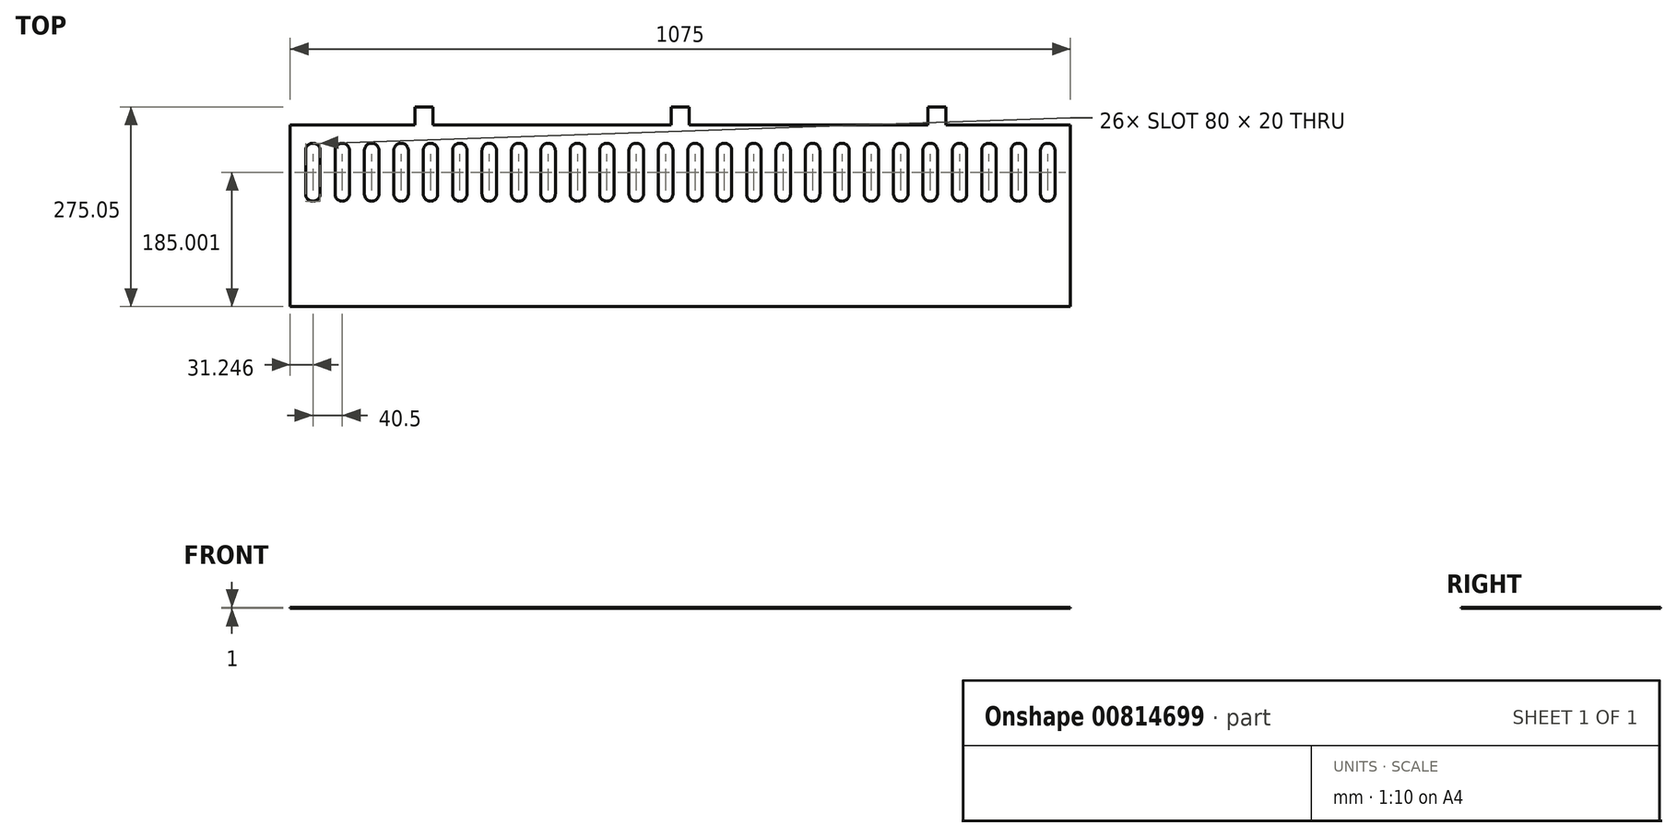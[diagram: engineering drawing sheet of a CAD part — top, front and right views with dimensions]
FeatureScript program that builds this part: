
annotation { "Feature Type Name" : "Feature", "Feature Type Description" : "" }
export const myFeature = defineFeature(function(context is Context, id is Id, definition is map)
    precondition{}
    {
        {
            var Q0;
            Q0=qCreatedBy(makeId("Top.planeOp"),FACE);
            var sketch = newSketch(context, id + "F0", { "sketchPlane" : qUnion([Q0])});
            skLineSegment(sketch, "E0.bottom", {"start": v(-117.32, -164.64) * mm, "end": v(957.68, -164.64) * mm});
            skLineSegment(sketch, "E0.top", {"start": v(-117.32, -414.64) * mm, "end": v(957.68, -414.64) * mm});
            skLineSegment(sketch, "E0.left", {"start": v(-117.32, -164.64) * mm, "end": v(-117.32, -414.64) * mm});
            skLineSegment(sketch, "E0.right", {"start": v(957.68, -164.64) * mm, "end": v(957.68, -414.64) * mm});
            skArc(sketch, "E1", {"start": v(-76.07, -199.64) * mm, "mid": v(-86.07, -189.64) * mm, "end": v(-96.07, -199.64) * mm});
            skArc(sketch, "E2", {"start": v(-96.07, -259.64) * mm, "mid": v(-86.07, -269.64) * mm, "end": v(-76.07, -259.64) * mm});
            skLineSegment(sketch, "E3", {"start": v(-96.07, -199.64) * mm, "end": v(-96.07, -259.64) * mm});
            skLineSegment(sketch, "E4", {"start": v(-76.07, -199.64) * mm, "end": v(-76.07, -259.64) * mm});
            skArc(sketch, "E5", {"start": v(-35.57, -199.64) * mm, "mid": v(-45.57, -189.64) * mm, "end": v(-55.57, -199.64) * mm});
            skArc(sketch, "E6", {"start": v(-55.57, -259.64) * mm, "mid": v(-45.57, -269.64) * mm, "end": v(-35.57, -259.64) * mm});
            skLineSegment(sketch, "E7", {"start": v(-55.57, -199.64) * mm, "end": v(-55.57, -259.64) * mm});
            skLineSegment(sketch, "E8", {"start": v(-35.57, -199.64) * mm, "end": v(-35.57, -259.64) * mm});
            skArc(sketch, "E9", {"start": v(4.93, -199.64) * mm, "mid": v(-5.07, -189.64) * mm, "end": v(-15.07, -199.64) * mm});
            skArc(sketch, "E10", {"start": v(-15.07, -259.64) * mm, "mid": v(-5.07, -269.64) * mm, "end": v(4.93, -259.64) * mm});
            skLineSegment(sketch, "E11", {"start": v(-15.07, -199.64) * mm, "end": v(-15.07, -259.64) * mm});
            skLineSegment(sketch, "E12", {"start": v(4.93, -199.64) * mm, "end": v(4.93, -259.64) * mm});
            skArc(sketch, "E13", {"start": v(45.43, -199.64) * mm, "mid": v(35.43, -189.64) * mm, "end": v(25.43, -199.64) * mm});
            skArc(sketch, "E14", {"start": v(25.43, -259.64) * mm, "mid": v(35.43, -269.64) * mm, "end": v(45.43, -259.64) * mm});
            skLineSegment(sketch, "E15", {"start": v(25.43, -199.64) * mm, "end": v(25.43, -259.64) * mm});
            skLineSegment(sketch, "E16", {"start": v(45.43, -199.64) * mm, "end": v(45.43, -259.64) * mm});
            skArc(sketch, "E17", {"start": v(85.93, -199.64) * mm, "mid": v(75.93, -189.64) * mm, "end": v(65.93, -199.64) * mm});
            skArc(sketch, "E18", {"start": v(65.93, -259.64) * mm, "mid": v(75.93, -269.64) * mm, "end": v(85.93, -259.64) * mm});
            skLineSegment(sketch, "E19", {"start": v(65.93, -199.64) * mm, "end": v(65.93, -259.64) * mm});
            skLineSegment(sketch, "E20", {"start": v(85.93, -199.64) * mm, "end": v(85.93, -259.64) * mm});
            skArc(sketch, "E21", {"start": v(126.43, -199.64) * mm, "mid": v(116.43, -189.64) * mm, "end": v(106.43, -199.64) * mm});
            skArc(sketch, "E22", {"start": v(106.43, -259.64) * mm, "mid": v(116.43, -269.64) * mm, "end": v(126.43, -259.64) * mm});
            skLineSegment(sketch, "E23", {"start": v(106.43, -199.64) * mm, "end": v(106.43, -259.64) * mm});
            skLineSegment(sketch, "E24", {"start": v(126.43, -199.64) * mm, "end": v(126.43, -259.64) * mm});
            skArc(sketch, "E25", {"start": v(207.43, -199.64) * mm, "mid": v(197.43, -189.64) * mm, "end": v(187.43, -199.64) * mm});
            skArc(sketch, "E26", {"start": v(187.43, -259.64) * mm, "mid": v(197.43, -269.64) * mm, "end": v(207.43, -259.64) * mm});
            skLineSegment(sketch, "E27", {"start": v(187.43, -199.64) * mm, "end": v(187.43, -259.64) * mm});
            skLineSegment(sketch, "E28", {"start": v(207.43, -199.64) * mm, "end": v(207.43, -259.64) * mm});
            skArc(sketch, "E29", {"start": v(247.93, -199.64) * mm, "mid": v(237.93, -189.64) * mm, "end": v(227.93, -199.64) * mm});
            skArc(sketch, "E30", {"start": v(227.93, -259.64) * mm, "mid": v(237.93, -269.64) * mm, "end": v(247.93, -259.64) * mm});
            skLineSegment(sketch, "E31", {"start": v(227.93, -199.64) * mm, "end": v(227.93, -259.64) * mm});
            skLineSegment(sketch, "E32", {"start": v(247.93, -199.64) * mm, "end": v(247.93, -259.64) * mm});
            skArc(sketch, "E33", {"start": v(288.43, -199.64) * mm, "mid": v(278.43, -189.64) * mm, "end": v(268.43, -199.64) * mm});
            skArc(sketch, "E34", {"start": v(268.43, -259.64) * mm, "mid": v(278.43, -269.64) * mm, "end": v(288.43, -259.64) * mm});
            skLineSegment(sketch, "E35", {"start": v(268.43, -199.64) * mm, "end": v(268.43, -259.64) * mm});
            skLineSegment(sketch, "E36", {"start": v(288.43, -199.64) * mm, "end": v(288.43, -259.64) * mm});
            skArc(sketch, "E37", {"start": v(328.93, -199.64) * mm, "mid": v(318.93, -189.64) * mm, "end": v(308.93, -199.64) * mm});
            skArc(sketch, "E38", {"start": v(308.93, -259.64) * mm, "mid": v(318.93, -269.64) * mm, "end": v(328.93, -259.64) * mm});
            skLineSegment(sketch, "E39", {"start": v(308.93, -199.64) * mm, "end": v(308.93, -259.64) * mm});
            skLineSegment(sketch, "E40", {"start": v(328.93, -199.64) * mm, "end": v(328.93, -259.64) * mm});
            skArc(sketch, "E41", {"start": v(369.43, -199.64) * mm, "mid": v(359.43, -189.64) * mm, "end": v(349.43, -199.64) * mm});
            skArc(sketch, "E42", {"start": v(349.43, -259.64) * mm, "mid": v(359.43, -269.64) * mm, "end": v(369.43, -259.64) * mm});
            skLineSegment(sketch, "E43", {"start": v(349.43, -199.64) * mm, "end": v(349.43, -259.64) * mm});
            skLineSegment(sketch, "E44", {"start": v(369.43, -199.64) * mm, "end": v(369.43, -259.64) * mm});
            skArc(sketch, "E45", {"start": v(409.93, -199.64) * mm, "mid": v(399.93, -189.64) * mm, "end": v(389.93, -199.64) * mm});
            skArc(sketch, "E46", {"start": v(389.93, -259.64) * mm, "mid": v(399.93, -269.64) * mm, "end": v(409.93, -259.64) * mm});
            skLineSegment(sketch, "E47", {"start": v(389.93, -199.64) * mm, "end": v(389.93, -259.64) * mm});
            skLineSegment(sketch, "E48", {"start": v(409.93, -199.64) * mm, "end": v(409.93, -259.64) * mm});
            skArc(sketch, "E49", {"start": v(450.43, -199.64) * mm, "mid": v(440.43, -189.64) * mm, "end": v(430.43, -199.64) * mm});
            skArc(sketch, "E50", {"start": v(430.43, -259.64) * mm, "mid": v(440.43, -269.64) * mm, "end": v(450.43, -259.64) * mm});
            skLineSegment(sketch, "E51", {"start": v(430.43, -199.64) * mm, "end": v(430.43, -259.64) * mm});
            skLineSegment(sketch, "E52", {"start": v(450.43, -199.64) * mm, "end": v(450.43, -259.64) * mm});
            skArc(sketch, "E53", {"start": v(490.93, -199.64) * mm, "mid": v(480.93, -189.64) * mm, "end": v(470.93, -199.64) * mm});
            skArc(sketch, "E54", {"start": v(470.93, -259.64) * mm, "mid": v(480.93, -269.64) * mm, "end": v(490.93, -259.64) * mm});
            skLineSegment(sketch, "E55", {"start": v(470.93, -199.64) * mm, "end": v(470.93, -259.64) * mm});
            skLineSegment(sketch, "E56", {"start": v(490.93, -199.64) * mm, "end": v(490.93, -259.64) * mm});
            skArc(sketch, "E57", {"start": v(531.43, -199.64) * mm, "mid": v(521.43, -189.64) * mm, "end": v(511.43, -199.64) * mm});
            skArc(sketch, "E58", {"start": v(511.43, -259.64) * mm, "mid": v(521.43, -269.64) * mm, "end": v(531.43, -259.64) * mm});
            skLineSegment(sketch, "E59", {"start": v(511.43, -199.64) * mm, "end": v(511.43, -259.64) * mm});
            skLineSegment(sketch, "E60", {"start": v(531.43, -199.64) * mm, "end": v(531.43, -259.64) * mm});
            skArc(sketch, "E61", {"start": v(166.93, -199.64) * mm, "mid": v(156.93, -189.64) * mm, "end": v(146.93, -199.64) * mm});
            skArc(sketch, "E62", {"start": v(146.93, -259.64) * mm, "mid": v(156.93, -269.64) * mm, "end": v(166.93, -259.64) * mm});
            skLineSegment(sketch, "E63", {"start": v(146.93, -199.64) * mm, "end": v(146.93, -259.64) * mm});
            skLineSegment(sketch, "E64", {"start": v(166.93, -199.64) * mm, "end": v(166.93, -259.64) * mm});
            skArc(sketch, "E65", {"start": v(612.43, -199.64) * mm, "mid": v(602.43, -189.64) * mm, "end": v(592.43, -199.64) * mm});
            skArc(sketch, "E66", {"start": v(592.43, -259.64) * mm, "mid": v(602.43, -269.64) * mm, "end": v(612.43, -259.64) * mm});
            skLineSegment(sketch, "E67", {"start": v(592.43, -199.64) * mm, "end": v(592.43, -259.64) * mm});
            skLineSegment(sketch, "E68", {"start": v(612.43, -199.64) * mm, "end": v(612.43, -259.64) * mm});
            skArc(sketch, "E69", {"start": v(652.93, -199.64) * mm, "mid": v(642.93, -189.64) * mm, "end": v(632.93, -199.64) * mm});
            skArc(sketch, "E70", {"start": v(632.93, -259.64) * mm, "mid": v(642.93, -269.64) * mm, "end": v(652.93, -259.64) * mm});
            skLineSegment(sketch, "E71", {"start": v(632.93, -199.64) * mm, "end": v(632.93, -259.64) * mm});
            skLineSegment(sketch, "E72", {"start": v(652.93, -199.64) * mm, "end": v(652.93, -259.64) * mm});
            skArc(sketch, "E73", {"start": v(693.43, -199.64) * mm, "mid": v(683.43, -189.64) * mm, "end": v(673.43, -199.64) * mm});
            skArc(sketch, "E74", {"start": v(673.43, -259.64) * mm, "mid": v(683.43, -269.64) * mm, "end": v(693.43, -259.64) * mm});
            skLineSegment(sketch, "E75", {"start": v(673.43, -199.64) * mm, "end": v(673.43, -259.64) * mm});
            skLineSegment(sketch, "E76", {"start": v(693.43, -199.64) * mm, "end": v(693.43, -259.64) * mm});
            skArc(sketch, "E77", {"start": v(733.93, -199.64) * mm, "mid": v(723.93, -189.64) * mm, "end": v(713.93, -199.64) * mm});
            skArc(sketch, "E78", {"start": v(713.93, -259.64) * mm, "mid": v(723.93, -269.64) * mm, "end": v(733.93, -259.64) * mm});
            skLineSegment(sketch, "E79", {"start": v(713.93, -199.64) * mm, "end": v(713.93, -259.64) * mm});
            skArc(sketch, "E80", {"start": v(774.43, -199.64) * mm, "mid": v(764.43, -189.64) * mm, "end": v(754.43, -199.64) * mm});
            skArc(sketch, "E81", {"start": v(754.43, -259.64) * mm, "mid": v(764.43, -269.64) * mm, "end": v(774.43, -259.64) * mm});
            skLineSegment(sketch, "E82", {"start": v(754.43, -199.64) * mm, "end": v(754.43, -259.64) * mm});
            skLineSegment(sketch, "E83", {"start": v(774.43, -199.64) * mm, "end": v(774.43, -259.64) * mm});
            skArc(sketch, "E84", {"start": v(814.93, -199.64) * mm, "mid": v(804.93, -189.64) * mm, "end": v(794.93, -199.64) * mm});
            skArc(sketch, "E85", {"start": v(794.93, -259.64) * mm, "mid": v(804.93, -269.64) * mm, "end": v(814.93, -259.64) * mm});
            skLineSegment(sketch, "E86", {"start": v(794.93, -199.64) * mm, "end": v(794.93, -259.64) * mm});
            skLineSegment(sketch, "E87", {"start": v(814.93, -199.64) * mm, "end": v(814.93, -259.64) * mm});
            skArc(sketch, "E88", {"start": v(855.43, -199.64) * mm, "mid": v(845.43, -189.64) * mm, "end": v(835.43, -199.64) * mm});
            skArc(sketch, "E89", {"start": v(835.43, -259.64) * mm, "mid": v(845.43, -269.64) * mm, "end": v(855.43, -259.64) * mm});
            skLineSegment(sketch, "E90", {"start": v(835.43, -199.64) * mm, "end": v(835.43, -259.64) * mm});
            skLineSegment(sketch, "E91", {"start": v(855.43, -199.64) * mm, "end": v(855.43, -259.64) * mm});
            skArc(sketch, "E92", {"start": v(895.93, -199.64) * mm, "mid": v(885.93, -189.64) * mm, "end": v(875.93, -199.64) * mm});
            skArc(sketch, "E93", {"start": v(875.93, -259.64) * mm, "mid": v(885.93, -269.64) * mm, "end": v(895.93, -259.64) * mm});
            skLineSegment(sketch, "E94", {"start": v(875.93, -199.64) * mm, "end": v(875.93, -259.64) * mm});
            skLineSegment(sketch, "E95", {"start": v(895.93, -199.64) * mm, "end": v(895.93, -259.64) * mm});
            skArc(sketch, "E96", {"start": v(936.43, -199.64) * mm, "mid": v(926.43, -189.64) * mm, "end": v(916.43, -199.64) * mm});
            skArc(sketch, "E97", {"start": v(916.43, -259.64) * mm, "mid": v(926.43, -269.64) * mm, "end": v(936.43, -259.64) * mm});
            skLineSegment(sketch, "E98", {"start": v(916.43, -199.64) * mm, "end": v(916.43, -259.64) * mm});
            skLineSegment(sketch, "E99", {"start": v(936.43, -199.64) * mm, "end": v(936.43, -259.64) * mm});
            skArc(sketch, "E100", {"start": v(571.93, -199.64) * mm, "mid": v(561.93, -189.64) * mm, "end": v(551.93, -199.64) * mm});
            skArc(sketch, "E101", {"start": v(551.93, -259.64) * mm, "mid": v(561.93, -269.64) * mm, "end": v(571.93, -259.64) * mm});
            skLineSegment(sketch, "E102", {"start": v(551.93, -199.64) * mm, "end": v(551.93, -259.64) * mm});
            skLineSegment(sketch, "E103", {"start": v(571.93, -199.64) * mm, "end": v(571.93, -259.64) * mm});
            skLineSegment(sketch, "E104", {"start": v(733.93, -199.64) * mm, "end": v(733.93, -259.64) * mm});
            skLineSegment(sketch, "E105", {"start": v(407.68, -164.64) * mm, "end": v(407.68, -139.64) * mm});
            skLineSegment(sketch, "E106", {"start": v(407.68, -139.64) * mm, "end": v(432.68, -139.64) * mm});
            skLineSegment(sketch, "E107", {"start": v(432.68, -139.64) * mm, "end": v(432.68, -164.64) * mm});
            skLineSegment(sketch, "E108", {"start": v(761, -164.64) * mm, "end": v(761, -139.6) * mm});
            skLineSegment(sketch, "E109", {"start": v(761, -139.6) * mm, "end": v(786, -139.6) * mm});
            skLineSegment(sketch, "E110", {"start": v(786, -139.6) * mm, "end": v(786, -164.64) * mm});
            skLineSegment(sketch, "E111", {"start": v(54.35, -164.64) * mm, "end": v(54.35, -139.64) * mm});
            skLineSegment(sketch, "E112", {"start": v(54.35, -139.64) * mm, "end": v(79.35, -139.64) * mm});
            skLineSegment(sketch, "E113", {"start": v(79.35, -139.64) * mm, "end": v(79.35, -164.64) * mm});
            skSolve(sketch);
        }
        {
            var Q0;
            Q0 = qSketchRegion(id + "F0", true);
            extrude(context, id + "F1", {"entities" : qUnion([Q0]), "depth" : 1 * mm, "offsetDistance" : 25 * mm});
        }
    });
